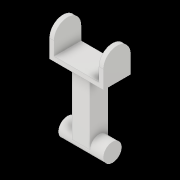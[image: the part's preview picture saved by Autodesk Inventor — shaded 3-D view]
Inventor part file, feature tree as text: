
AUTODESK INVENTOR PART (.ipt)
format: ipt  version: 2019 (Build 230136000, 136)  size: 119,296 bytes
history: native  units: mm
features: extrude x4, sketch x4, mirror x1
ambient origin geometry x8: Origin, YZ Plane, XZ Plane, XY Plane, X Axis, Y Axis, Z Axis, Center Point
bodies: Body1 (feature_tree)
feature tree (9):
  extrude  "돌출7"  Depth=20.0mm
  extrude  "돌출8"  Depth=50.0mm TaperAngle=0.0deg
  extrude  "돌출9"  Depth=20.0mm
  extrude  "돌출10"  Depth=15.0mm
  mirror  "미러3"
  sketch  "스케치7"
  sketch  "스케치8"
  sketch  "스케치9"
  sketch  "스케치10"
